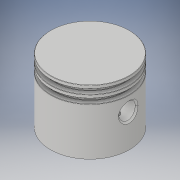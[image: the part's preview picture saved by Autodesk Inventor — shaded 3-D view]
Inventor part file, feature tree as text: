
AUTODESK INVENTOR PART (.ipt)
format: ipt  version: 2018 (Build 220112000, 112)  size: 293,376 bytes
history: native  units: mm
features: sketch x4, extrude x2, revolve x1, chamfer x1, hole x1, fillet x1
ambient origin geometry x8: Origin, YZ Plane, XZ Plane, XY Plane, X Axis, Y Axis, Z Axis, Center Point
bodies: Solid1 (feature_tree)
feature tree (10):
  revolve  "Revolution1"  [1 undecoded]
  extrude  "Extrusion1"  Depth=1.0mm
  extrude  "Extrusion2"  Depth=5.0mm
  chamfer  "Chamfer1"  Distance=0.1mm
  hole  "Hole1"  [1 undecoded]
  fillet  "Fillet1"  Radius=0.1mm
  sketch  "Sketch1"  dims[d0=12.0mm d3=1.0mm]
  sketch  "Sketch2"  dims[d4=1.5mm d5=1.0mm]
  sketch  "Sketch3"  dims[d6=1.5mm d7=5.0mm]
  sketch  "Sketch4"  dims[d8=1.0mm d9=0.1mm d10=19.5mm d11=0.1mm d12=90.0deg d13=10.0mm d14=5.0mm d15=11.0mm d16=0.0mm d17=5.0mm d18=10.0mm d19=36.75mm d20=0.0mm d21=0.5mm d22=2.0mm d23=45.0deg d24=8.0mm d25=8.0mm d26=2.013mm d27=5.0mm d28=4.0mm d29=2.0mm d30=90.0deg d31=7.6mm d32=0.0mm d33=1.0mm]
note: 2 required parameter values undecoded (feature->parameter linkage not recoverable at this tier; creation-order binding heuristic only, values carry confidence <= 0.55)